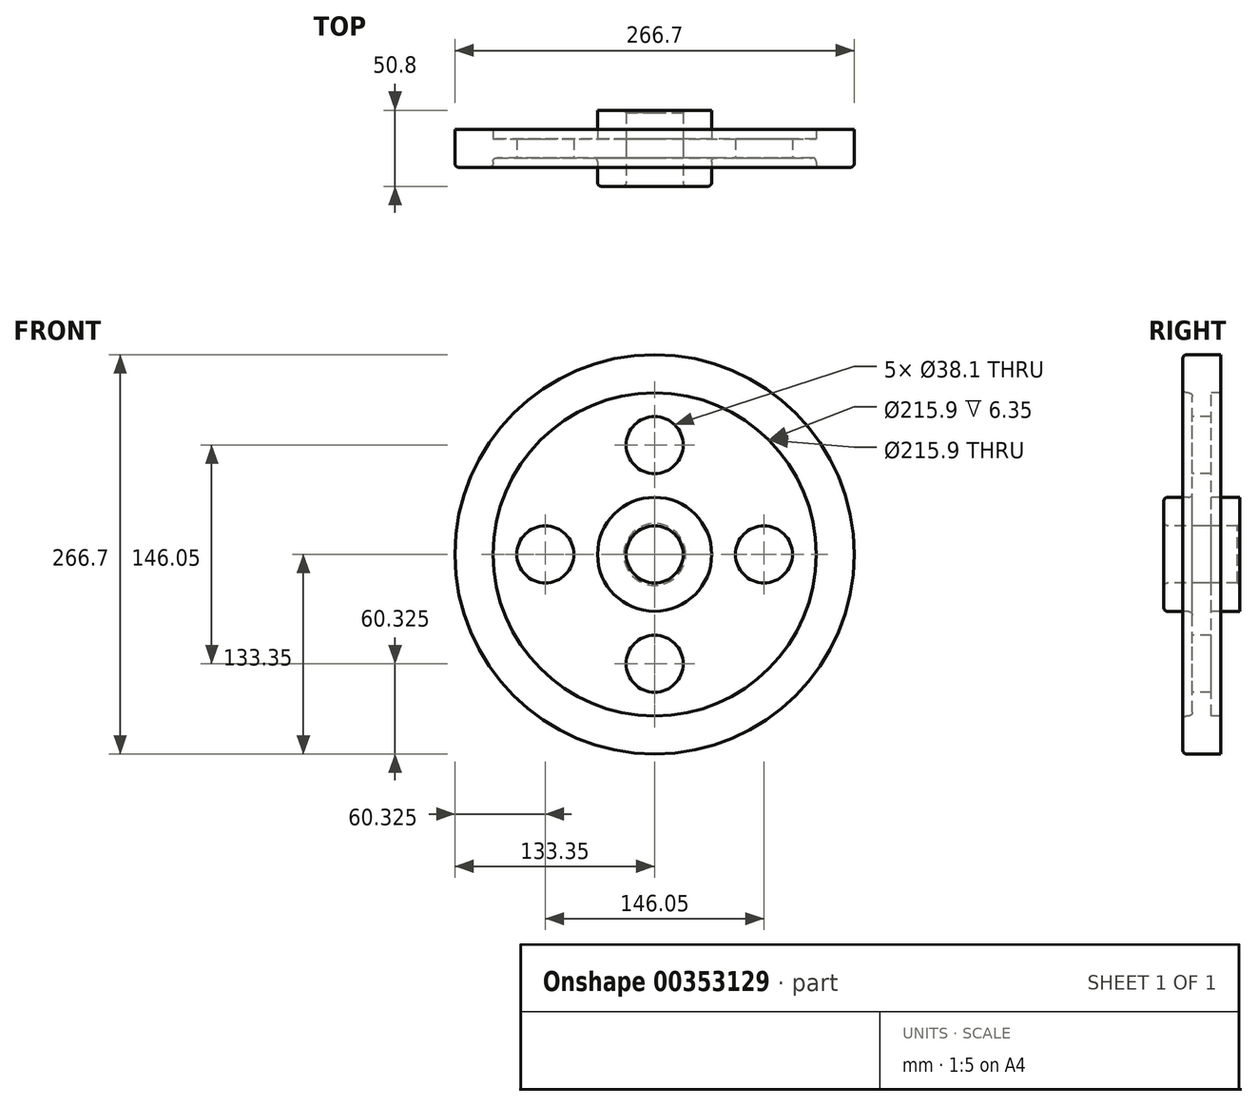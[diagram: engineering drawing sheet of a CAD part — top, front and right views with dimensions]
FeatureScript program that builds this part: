
annotation { "Feature Type Name" : "Feature", "Feature Type Description" : "" }
export const myFeature = defineFeature(function(context is Context, id is Id, definition is map)
    precondition{}
    {
        {
            var Q0;
            Q0=qCreatedBy(makeId("Right.planeOp"),FACE);
            var sketch = newSketch(context, id + "F0", { "sketchPlane" : qUnion([Q0])});
            skLineSegment(sketch, "E0", {"start": v(0, 0) * mm, "end": v(6.35, 0) * mm, "construction": true});
            skLineSegment(sketch, "E1.0", {"start": v(0, 19.05) * mm, "end": v(25.4, 19.05) * mm});
            skLineSegment(sketch, "E2.0", {"start": v(6.35, 38.1) * mm, "end": v(25.4, 38.1) * mm});
            skLineSegment(sketch, "E3.0", {"start": v(6.35, 107.95) * mm, "end": v(12.7, 107.95) * mm});
            skLineSegment(sketch, "E4.0", {"start": v(0, 133.35) * mm, "end": v(12.7, 133.35) * mm});
            skLineSegment(sketch, "E5", {"start": v(0, -1.82) * mm, "end": v(0, 133.35) * mm, "construction": true});
            skLineSegment(sketch, "E6.0", {"start": v(25.4, -1.82) * mm, "end": v(25.4, 0) * mm});
            skLineSegment(sketch, "E7.0", {"start": v(6.35, -1.82) * mm, "end": v(6.35, 0) * mm});
            skLineSegment(sketch, "E8.0", {"start": v(12.7, -1.82) * mm, "end": v(12.7, 0) * mm});
            skLineSegment(sketch, "E9.trimOffspring", {"start": v(12.7, 107.95) * mm, "end": v(12.7, 133.35) * mm});
            skLineSegment(sketch, "E10.trimOffspring", {"start": v(6.35, 38.1) * mm, "end": v(6.35, 107.95) * mm});
            skLineSegment(sketch, "E11.trimOffspring", {"start": v(25.4, 19.05) * mm, "end": v(25.4, 38.1) * mm});
            skLineSegment(sketch, "E12.MirrorCS", {"start": v(0, 133.35) * mm, "end": v(-12.7, 133.35) * mm});
            skLineSegment(sketch, "E13.MirrorCS", {"start": v(-12.7, 107.95) * mm, "end": v(-12.7, 133.35) * mm});
            skLineSegment(sketch, "E14.MirrorCS", {"start": v(-6.35, 107.95) * mm, "end": v(-12.7, 107.95) * mm});
            skLineSegment(sketch, "E15.MirrorCS", {"start": v(-6.35, 38.1) * mm, "end": v(-6.35, 107.95) * mm});
            skLineSegment(sketch, "E16.MirrorCS", {"start": v(-6.35, 38.1) * mm, "end": v(-25.4, 38.1) * mm});
            skLineSegment(sketch, "E17.MirrorCS", {"start": v(-25.4, 19.05) * mm, "end": v(-25.4, 38.1) * mm});
            skLineSegment(sketch, "E18.MirrorCS", {"start": v(0, 19.05) * mm, "end": v(-25.4, 19.05) * mm});
            skLineSegment(sketch, "E19", {"start": v(0, 0) * mm, "end": v(130.2, 0) * mm, "construction": true});
            skSolve(sketch);
        }
        {
            var Q0;
            Q0=makeQuery(id+"F0.imprint","IMPRINT",FACE,{"disambiguationData":[TD([[makeQuery(id+"F0.imprint","IMPRINT",EDGE,{"derivedFrom":sQuery(id+"F0.wireOp",EDGE,"E1.0")}),1.0]])]});
            var Q1;
            Q1=sQuery(id+"F0.wireOp",EDGE,"E19");
            revolve(context, id + "F1", {"entities" : qUnion([Q0]), "axis" : qUnion([Q1]), "revolveType" : RevolveType.FULL});
        }
        {
            var Q0;
            Q0=makeQuery(id+"F1.opRevolve","SWEPT_FACE",FACE,{"disambiguationData":[OSD([sQuery(id+"F0.wireOp",EDGE,"E15.MirrorCS")])]});
            var sketch = newSketch(context, id + "F2", { "sketchPlane" : qUnion([Q0])});
            skLineSegment(sketch, "E20", {"start": v(0, 0) * mm, "end": v(0, 73.03) * mm});
            skCircle(sketch, "E21", {"center": v(0, 73.03) * mm, "radius": 19.05 * mm});
            skCircle(sketch, "E22.1.0", {"center": v(-73.03, 0) * mm, "radius": 19.05 * mm});
            skCircle(sketch, "E22.2.0", {"center": v(0, -73.03) * mm, "radius": 19.05 * mm});
            skCircle(sketch, "E22.3.0", {"center": v(73.03, 0) * mm, "radius": 19.05 * mm});
            skPoint(sketch, "E22.center", {"position": v(0, 0) * mm});
            skSolve(sketch);
        }
        {
            var Q0;
            Q0=makeQuery(id+"F2.imprint","IMPRINT",FACE,{"disambiguationData":[TD([[makeQuery(id+"F2.imprint","IMPRINT",EDGE,{"derivedFrom":sQuery(id+"F2.wireOp",EDGE,"E22.1.0")}),1.0]])]});
            var Q1;
            Q1=makeQuery(id+"F2.imprint","IMPRINT",FACE,{"disambiguationData":[TD([[makeQuery(id+"F2.imprint","IMPRINT",EDGE,{"derivedFrom":sQuery(id+"F2.wireOp",EDGE,"E21")}),1.0]])]});
            var Q2;
            Q2=makeQuery(id+"F2.imprint","IMPRINT",FACE,{"disambiguationData":[TD([[makeQuery(id+"F2.imprint","IMPRINT",EDGE,{"derivedFrom":sQuery(id+"F2.wireOp",EDGE,"E22.3.0")}),1.0]])]});
            var Q3;
            Q3=makeQuery(id+"F2.imprint","IMPRINT",FACE,{"disambiguationData":[TD([[makeQuery(id+"F2.imprint","IMPRINT",EDGE,{"derivedFrom":sQuery(id+"F2.wireOp",EDGE,"E22.2.0")}),1.0]])]});
            extrude(context, id + "F3", {"entities" : qUnion([Q0, Q1, Q2, Q3]), "operationType" : NewBodyOperationType.REMOVE, "oppositeDirection" : true, "depth" : 25.4 * mm});
        }
        {
            var Q0;
            Q0=makeQuery(id+"F1.opRevolve","SWEPT_EDGE",EDGE,{"disambiguationData":[OSD([sQuery(id+"F0.wireOp",EDGE,"E15.MirrorCS"),sQuery(id+"F0.wireOp",EDGE,"E16.MirrorCS")])]});
            var Q1;
            Q1=makeQuery(id+"F1.opRevolve","SWEPT_FACE",FACE,{"disambiguationData":[OSD([sQuery(id+"F0.wireOp",EDGE,"E14.MirrorCS")])]});
            var Q2;
            Q2=makeQuery(id+"F1.opRevolve","SWEPT_FACE",FACE,{"disambiguationData":[OSD([sQuery(id+"F0.wireOp",EDGE,"E13.MirrorCS")])]});
            var Q3;
            Q3=makeQuery(id+"F1.opRevolve","SWEPT_FACE",FACE,{"disambiguationData":[OSD([sQuery(id+"F0.wireOp",EDGE,"E17.MirrorCS")])]});
            fillet(context, id + "F4", {"entities" : qUnion([Q0, Q1, Q2, Q3]), "radius" : 2.54 * mm, "tangentPropagation" : true, "allowEdgeOverflow" : false});
        }
        {
            var Q0;
            Q0=makeQuery(id+"F1.opRevolve","SWEPT_FACE",FACE,{"disambiguationData":[OSD([sQuery(id+"F0.wireOp",EDGE,"E1.0"),sQuery(id+"F0.wireOp",EDGE,"E18.MirrorCS")])]});
            chamfer(context, id + "F5", {"entities" : qUnion([Q0]), "width" : 1.59 * mm, "tangentPropagation" : true});
        }
    });
